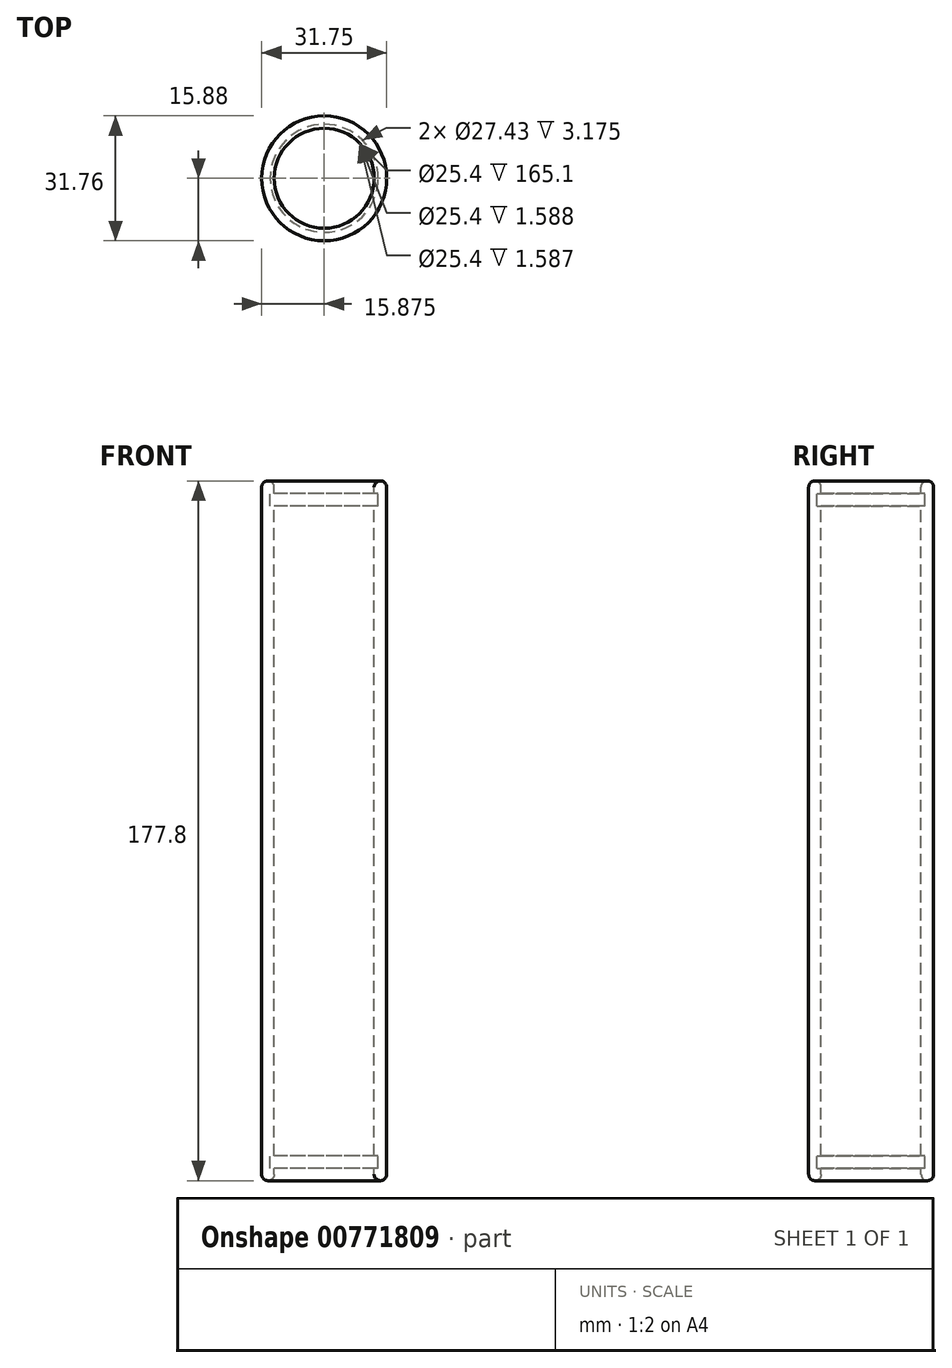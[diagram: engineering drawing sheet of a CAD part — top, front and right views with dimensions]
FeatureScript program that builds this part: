
annotation { "Feature Type Name" : "Feature", "Feature Type Description" : "" }
export const myFeature = defineFeature(function(context is Context, id is Id, definition is map)
    precondition{}
    {
        {
            var Q0;
            Q0=qCreatedBy(makeId("Front.planeOp"),FACE);
            var sketch = newSketch(context, id + "F0", { "sketchPlane" : qUnion([Q0])});
            skLineSegment(sketch, "E0.left", {"start": v(0, 114.3) * mm, "end": v(0, 201.61) * mm});
            skLineSegment(sketch, "E0.right", {"start": v(3.17, 114.3) * mm, "end": v(3.17, 196.85) * mm});
            skLineSegment(sketch, "E1", {"start": v(3.17, 203.2) * mm, "end": v(15.87, 203.2) * mm, "construction": true});
            skLineSegment(sketch, "E2", {"start": v(15.87, 203.2) * mm, "end": v(15.87, 114.3) * mm, "construction": true});
            skArc(sketch, "E3", {"start": v(3.17, 201.61) * mm, "mid": v(1.59, 203.2) * mm, "end": v(0, 201.61) * mm});
            skPoint(sketch, "E3.startSnap0", {"position": v(1.59, 201.61) * mm});
            skPoint(sketch, "E3.endSnap0", {"position": v(1.59, 201.61) * mm});
            skPoint(sketch, "E4.orphan", {"position": v(1.59, 200.03) * mm});
            skPoint(sketch, "E5.start.orphan", {"position": v(1.59, 203.2) * mm});
            skLineSegment(sketch, "E6", {"start": v(3.17, 200.03) * mm, "end": v(2.16, 200.03) * mm});
            skLineSegment(sketch, "E7", {"start": v(2.16, 200.03) * mm, "end": v(2.16, 196.85) * mm});
            skLineSegment(sketch, "E8", {"start": v(2.16, 196.85) * mm, "end": v(3.17, 196.85) * mm});
            skLineSegment(sketch, "E9.trimOffspring", {"start": v(3.17, 200.03) * mm, "end": v(3.17, 201.61) * mm});
            skLineSegment(sketch, "E10.MirrorCS", {"start": v(3.17, 28.58) * mm, "end": v(3.17, 26.99) * mm});
            skLineSegment(sketch, "E11.MirrorCS", {"start": v(3.17, 28.58) * mm, "end": v(2.16, 28.58) * mm});
            skArc(sketch, "E12.MirrorCS", {"start": v(3.17, 26.99) * mm, "mid": v(1.59, 25.4) * mm, "end": v(0, 26.99) * mm});
            skLineSegment(sketch, "E13.MirrorCS", {"start": v(2.16, 28.57) * mm, "end": v(2.16, 31.75) * mm});
            skLineSegment(sketch, "E14.MirrorCS", {"start": v(2.16, 31.75) * mm, "end": v(3.17, 31.75) * mm});
            skLineSegment(sketch, "E15.MirrorCS", {"start": v(15.87, 25.4) * mm, "end": v(15.87, 114.3) * mm, "construction": true});
            skPoint(sketch, "E16.MirrorP", {"position": v(1.59, 28.58) * mm});
            skLineSegment(sketch, "E17.MirrorCS", {"start": v(3.17, 114.3) * mm, "end": v(3.17, 31.75) * mm});
            skLineSegment(sketch, "E18.MirrorCS", {"start": v(0, 114.3) * mm, "end": v(0, 26.99) * mm});
            skPoint(sketch, "E19.MirrorP", {"position": v(1.59, 25.4) * mm});
            skLineSegment(sketch, "E20", {"start": v(15.87, 25.4) * mm, "end": v(0, 0) * mm});
            skSolve(sketch);
        }
        {
            var Q0;
            Q0=makeQuery(id+"F0.imprint","IMPRINT",FACE,{"disambiguationData":[TD([[makeQuery(id+"F0.imprint","IMPRINT",EDGE,{"derivedFrom":sQuery(id+"F0.wireOp",EDGE,"E0.left")}),-1.0]])]});
            var Q1;
            Q1=sQuery(id+"F0.wireOp",EDGE,"E2");
            revolve(context, id + "F1", {"surfaceOperationType" : NewSurfaceOperationType.NEW, "entities" : qUnion([Q0]), "axis" : qUnion([Q1]), "revolveType" : RevolveType.FULL});
        }
    });
